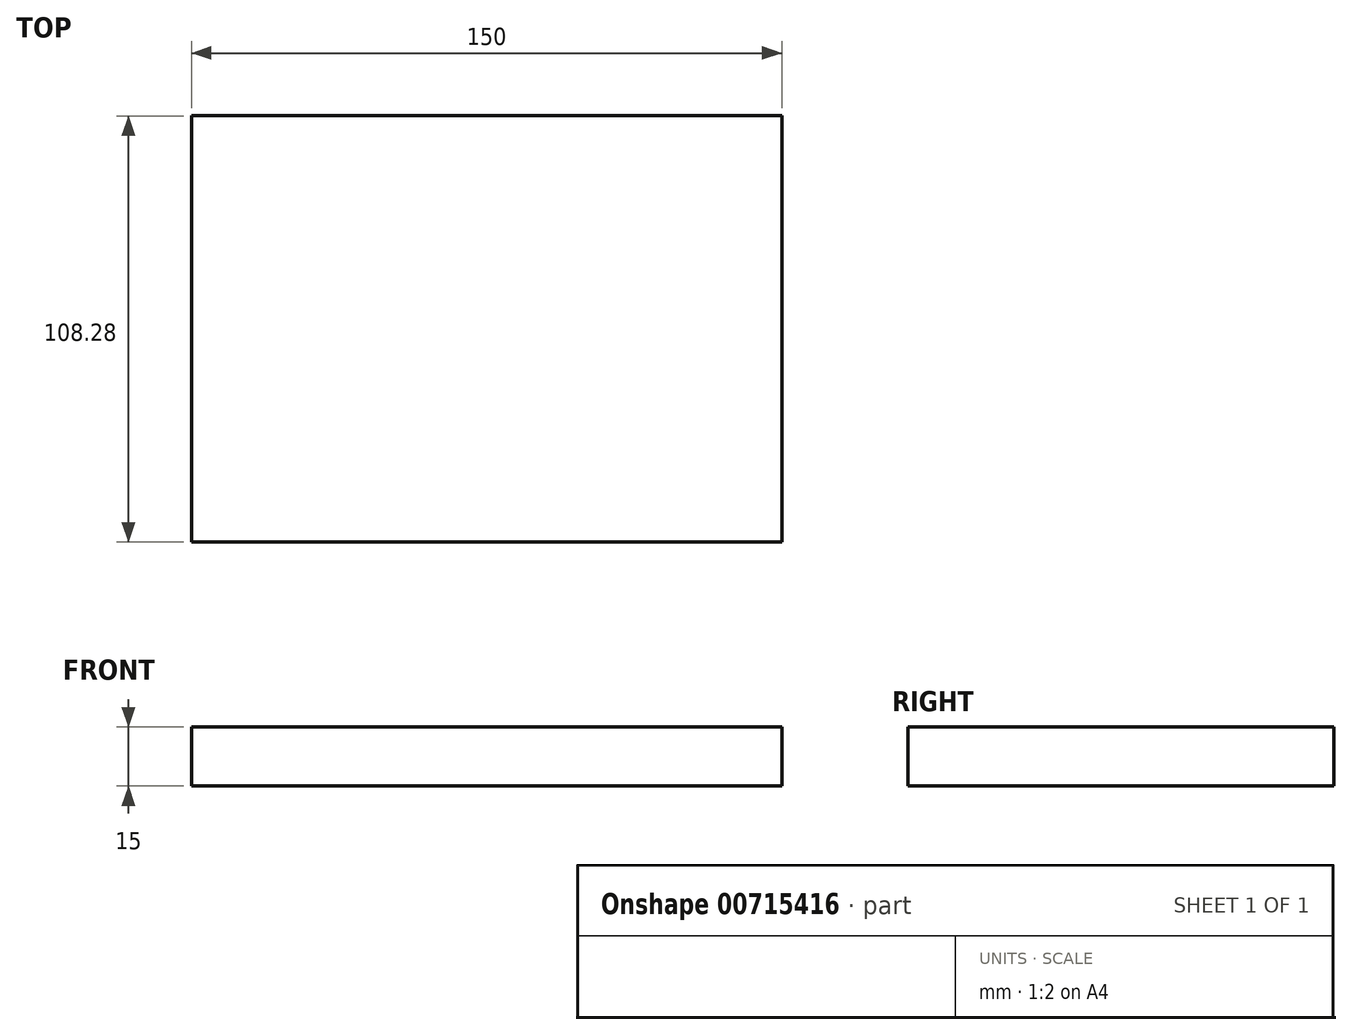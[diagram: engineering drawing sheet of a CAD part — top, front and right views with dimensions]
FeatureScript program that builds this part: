
annotation { "Feature Type Name" : "Feature", "Feature Type Description" : "" }
export const myFeature = defineFeature(function(context is Context, id is Id, definition is map)
    precondition{}
    {
        {
            var Q0;
            Q0=qCreatedBy(makeId("Top.planeOp"),FACE);
            var sketch = newSketch(context, id + "F0", { "sketchPlane" : qUnion([Q0])});
            skLineSegment(sketch, "E0.bottom", {"start": v(-75, 44.05) * mm, "end": v(75, 44.05) * mm});
            skLineSegment(sketch, "E0.top", {"start": v(-75, -64.23) * mm, "end": v(75, -64.23) * mm});
            skLineSegment(sketch, "E0.left", {"start": v(-75, 44.05) * mm, "end": v(-75, -64.23) * mm});
            skLineSegment(sketch, "E0.right", {"start": v(75, 44.05) * mm, "end": v(75, -64.23) * mm});
            skSolve(sketch);
        }
        {
            var Q0;
            Q0 = qSketchRegion(id + "F0", true);
            extrude(context, id + "F1", {"entities" : qUnion([Q0]), "depth" : 15 * mm, "offsetDistance" : 25 * mm});
        }
    });
